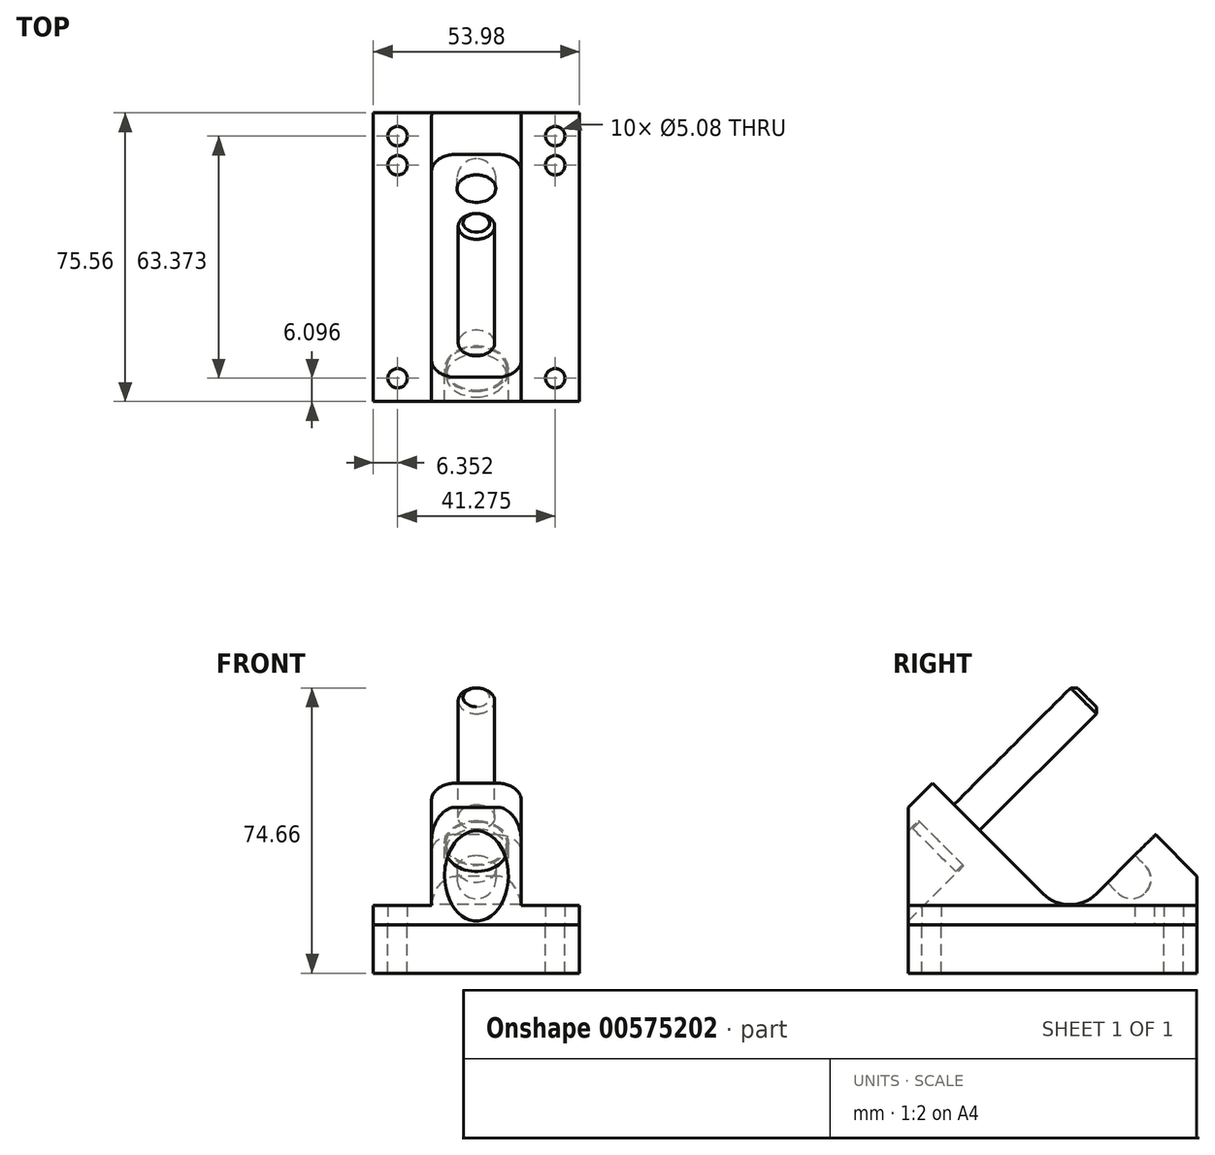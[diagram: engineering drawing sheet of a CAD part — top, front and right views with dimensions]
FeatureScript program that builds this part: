
annotation { "Feature Type Name" : "Feature", "Feature Type Description" : "" }
export const myFeature = defineFeature(function(context is Context, id is Id, definition is map)
    precondition{}
    {
        {
            var Q0;
            Q0=qCreatedBy(makeId("Right.planeOp"),FACE);
            var sketch = newSketch(context, id + "F0", { "sketchPlane" : qUnion([Q0])});
            skLineSegment(sketch, "E0", {"start": v(0, 0) * mm, "end": v(75.57, 0) * mm});
            skLineSegment(sketch, "E1", {"start": v(75.57, 0) * mm, "end": v(75.57, 12.7) * mm});
            skLineSegment(sketch, "E2", {"start": v(75.57, 12.7) * mm, "end": v(64.7, 23.57) * mm});
            skLineSegment(sketch, "E3", {"start": v(64.7, 23.57) * mm, "end": v(42.25, 1.12) * mm});
            skLineSegment(sketch, "E4", {"start": v(0, -14.12) * mm, "end": v(0, 0) * mm, "construction": true});
            skLineSegment(sketch, "E5", {"start": v(0, 0) * mm, "end": v(0, 30.72) * mm});
            skLineSegment(sketch, "E6", {"start": v(0, 30.72) * mm, "end": v(6.32, 37.04) * mm});
            skLineSegment(sketch, "E7", {"start": v(6.32, 37.04) * mm, "end": v(42.25, 1.12) * mm});
            skLineSegment(sketch, "E8", {"start": v(61.1, 19.98) * mm, "end": v(70.08, 11) * mm, "construction": true});
            skLineSegment(sketch, "E9", {"start": v(70.08, 11) * mm, "end": v(59.3, 0.22) * mm, "construction": true});
            skLineSegment(sketch, "E10", {"start": v(59.3, 0.22) * mm, "end": v(50.33, 9.2) * mm, "construction": true});
            skLineSegment(sketch, "E11", {"start": v(64.7, 5.6) * mm, "end": v(15.3, 55) * mm, "construction": true});
            skCircle(sketch, "E12", {"center": v(15.3, 55) * mm, "radius": 4 * mm, "construction": true});
            skLineSegment(sketch, "E13", {"start": v(15.3, 28.06) * mm, "end": v(28.77, 41.53) * mm, "construction": true});
            skCircle(sketch, "E14", {"center": v(58.4, 11.9) * mm, "radius": 5.08 * mm, "construction": true});
            skSolve(sketch);
        }
        {
            var Q0;
            Q0=qSketchRegion(id+"F0",true);
            extrude(context, id + "F1", {"entities" : qUnion([Q0]), "depth" : 26.99 * mm});
        }
        {
            var Q0;
            Q0=makeQuery(id+"F1.opExtrude","SWEPT_EDGE",EDGE,{"disambiguationData":[OSD([sQuery(id+"F0.wireOp",EDGE,"E3"),sQuery(id+"F0.wireOp",EDGE,"E7")])]});
            fillet(context, id + "F2", {"entities" : qUnion([Q0]), "radius" : 9.9 * mm, "tangentPropagation" : true, "allowEdgeOverflow" : false});
        }
        {
            var Q0;
            Q0=makeQuery(id+"F1.opExtrude","CAP_FACE",FACE,{"disambiguationData":[OSD([sQuery(id+"F0.wireOp",EDGE,"E0"),sQuery(id+"F0.wireOp",EDGE,"E1"),sQuery(id+"F0.wireOp",EDGE,"E2"),sQuery(id+"F0.wireOp",EDGE,"E3"),sQuery(id+"F0.wireOp",EDGE,"O8t1L6aE-7V4B-qQYz-aJHa-yxt4Uf4GNHZm"),sQuery(id+"F0.wireOp",EDGE,"dINw5n4X-CGaa-rPGi-QK1T-MrZfrRMsY7ox"),sQuery(id+"F0.wireOp",EDGE,"k2Hi1M4v-dZXO-cidX-ee3S-7WINr6mVTnzP")])],"isStart":false});
            var sketch = newSketch(context, id + "F3", { "sketchPlane" : qUnion([Q0])});
            skLineSegment(sketch, "E15.bottom", {"start": v(75.57, 5.08) * mm, "end": v(0, 5.08) * mm});
            skLineSegment(sketch, "E15.top", {"start": v(75.57, 37.04) * mm, "end": v(0, 37.04) * mm});
            skLineSegment(sketch, "E15.left", {"start": v(75.57, 5.08) * mm, "end": v(75.57, 37.04) * mm});
            skLineSegment(sketch, "E15.right", {"start": v(0, 5.08) * mm, "end": v(0, 37.04) * mm});
            skSolve(sketch);
        }
        {
            var Q0;
            Q0=qSketchRegion(id+"F3",true);
            extrude(context, id + "F4", {"entities" : qUnion([Q0]), "operationType" : NewBodyOperationType.REMOVE, "oppositeDirection" : true, "depth" : 15.24 * mm});
        }
        {
            var Q0;
            Q0=makeQuery(id+"F1.opExtrude","SWEPT_FACE",FACE,{"disambiguationData":[OSD([sQuery(id+"F0.wireOp",EDGE,"E0")])]});
            var sketch = newSketch(context, id + "F5", { "sketchPlane" : qUnion([Q0])});
            skLineSegment(sketch, "E16", {"start": v(20.64, -6.1) * mm, "end": v(20.64, -61.85) * mm, "construction": true});
            skLineSegment(sketch, "E17", {"start": v(20.64, -61.85) * mm, "end": v(20.64, -69.47) * mm, "construction": true});
            skCircle(sketch, "E18", {"center": v(20.64, -6.1) * mm, "radius": 2.54 * mm});
            skCircle(sketch, "E19", {"center": v(20.64, -61.85) * mm, "radius": 2.54 * mm});
            skCircle(sketch, "E20", {"center": v(20.64, -69.47) * mm, "radius": 2.54 * mm});
            skSolve(sketch);
        }
        {
            var Q0;
            Q0=qSketchRegion(id+"F5",true);
            extrude(context, id + "F6", {"entities" : qUnion([Q0]), "operationType" : NewBodyOperationType.REMOVE, "endBound" : BoundingType.UP_TO_NEXT, "oppositeDirection" : true, "depth" : 25.4 * mm});
        }
        {
            var Q0;
            Q0=makeQuery(id+"F1.opExtrude","CAP_FACE",FACE,{"disambiguationData":[OSD([sQuery(id+"F0.wireOp",EDGE,"E0"),sQuery(id+"F0.wireOp",EDGE,"E1"),sQuery(id+"F0.wireOp",EDGE,"E2"),sQuery(id+"F0.wireOp",EDGE,"E3"),sQuery(id+"F0.wireOp",EDGE,"O8t1L6aE-7V4B-qQYz-aJHa-yxt4Uf4GNHZm"),sQuery(id+"F0.wireOp",EDGE,"dINw5n4X-CGaa-rPGi-QK1T-MrZfrRMsY7ox"),sQuery(id+"F0.wireOp",EDGE,"k2Hi1M4v-dZXO-cidX-ee3S-7WINr6mVTnzP")])],"isStart":true});
            var sketch = newSketch(context, id + "F7", { "sketchPlane" : qUnion([Q0])});
            skLineSegment(sketch, "E21", {"start": v(-11.94, 31.43) * mm, "end": v(-5.2, 24.7) * mm});
            skLineSegment(sketch, "E22", {"start": v(-5.2, 24.7) * mm, "end": v(-2.67, 27.22) * mm});
            skLineSegment(sketch, "E23", {"start": v(-2.67, 27.22) * mm, "end": v(12.28, 12.28) * mm});
            skLineSegment(sketch, "E24", {"start": v(12.28, 12.28) * mm, "end": v(6.38, 6.38) * mm});
            skLineSegment(sketch, "E25", {"start": v(6.38, 6.38) * mm, "end": v(-15.3, 28.06) * mm});
            skLineSegment(sketch, "E26", {"start": v(-15.3, 28.06) * mm, "end": v(-16.61, 29.37) * mm, "construction": true});
            skLineSegment(sketch, "E27", {"start": v(-15.3, 28.06) * mm, "end": v(-11.94, 31.43) * mm});
            skLineSegment(sketch, "E28", {"start": v(0, 0) * mm, "end": v(6.38, 6.38) * mm});
            skSolve(sketch);
        }
        {
            var Q0;
            Q0=qSketchRegion(id+"F7",true);
            var Q1;
            Q1=sQuery(id+"F7.wireOp",EDGE,"E25");
            revolve(context, id + "F8", {"operationType" : NewBodyOperationType.REMOVE, "entities" : qUnion([Q0]), "axis" : qUnion([Q1]), "revolveType" : RevolveType.FULL, "oppositeDirection" : true});
        }
        {
            var Q0;
            Q0=qCreatedBy(makeId("Right.planeOp"),FACE);
            var sketch = newSketch(context, id + "F9", { "sketchPlane" : qUnion([Q0])});
            skLineSegment(sketch, "E29", {"start": v(2.96, 26.94) * mm, "end": v(5.2, 24.7) * mm});
            skLineSegment(sketch, "E30", {"start": v(5.2, 24.7) * mm, "end": v(43.37, 62.86) * mm});
            skLineSegment(sketch, "E31", {"start": v(43.37, 62.86) * mm, "end": v(46.74, 59.5) * mm});
            skLineSegment(sketch, "E32", {"start": v(46.74, 59.5) * mm, "end": v(6.77, 19.53) * mm});
            skLineSegment(sketch, "E33", {"start": v(6.77, 19.53) * mm, "end": v(1.16, 25.14) * mm});
            skLineSegment(sketch, "E34", {"start": v(1.16, 25.14) * mm, "end": v(2.96, 26.94) * mm});
            skLineSegment(sketch, "E35", {"start": v(6.77, 19.53) * mm, "end": v(2.3, 15.06) * mm, "construction": true});
            skPoint(sketch, "E36", {"position": v(8.78, 21.53) * mm});
            skSolve(sketch);
        }
        {
            var Q0;
            Q0=qSketchRegion(id+"F9",true);
            var Q1;
            Q1=sQuery(id+"F9.wireOp",EDGE,"E32");
            revolve(context, id + "F10", {"entities" : qUnion([Q0]), "axis" : qUnion([Q1]), "revolveType" : RevolveType.FULL});
        }
        {
            var Q0;
            Q0=makeQuery(id+"F4.boolean.opBoolean","INTERSECT",EDGE,{"derivedFrom":[makeQuery(id+"F1.opExtrude","SWEPT_FACE",FACE,{"disambiguationData":[OSD([sQuery(id+"F0.wireOp",EDGE,"E2")])]}),makeQuery(id+"F4.opExtrude","CAP_FACE",FACE,{"disambiguationData":[OSD([sQuery(id+"F3.wireOp",EDGE,"E15.bottom"),sQuery(id+"F3.wireOp",EDGE,"E15.top"),sQuery(id+"F3.wireOp",EDGE,"E15.left"),sQuery(id+"F3.wireOp",EDGE,"E15.right")])],"isStart":false})]});
            var Q1;
            Q1=makeQuery(id+"FPWNDdPn0RB2iZ7_1.opPattern","COPY",EDGE,{"derivedFrom":makeQuery(id+"F4.boolean.opBoolean","INTERSECT",EDGE,{"derivedFrom":[makeQuery(id+"F1.opExtrude","SWEPT_FACE",FACE,{"disambiguationData":[OSD([sQuery(id+"F0.wireOp",EDGE,"E2")])]}),makeQuery(id+"F4.opExtrude","CAP_FACE",FACE,{"disambiguationData":[OSD([sQuery(id+"F3.wireOp",EDGE,"E15.bottom"),sQuery(id+"F3.wireOp",EDGE,"E15.top"),sQuery(id+"F3.wireOp",EDGE,"E15.left"),sQuery(id+"F3.wireOp",EDGE,"E15.right")])],"isStart":false})]}),"instanceName":"1"});
            var Q2;
            Q2=makeQuery(id+"F4.boolean.opBoolean","INTERSECT",EDGE,{"derivedFrom":[makeQuery(id+"F1.opExtrude","SWEPT_FACE",FACE,{"disambiguationData":[OSD([sQuery(id+"F0.wireOp",EDGE,"E6")])]}),makeQuery(id+"F4.opExtrude","CAP_FACE",FACE,{"disambiguationData":[OSD([sQuery(id+"F3.wireOp",EDGE,"E15.bottom"),sQuery(id+"F3.wireOp",EDGE,"E15.top"),sQuery(id+"F3.wireOp",EDGE,"E15.left"),sQuery(id+"F3.wireOp",EDGE,"E15.right")])],"isStart":false})]});
            var Q3;
            Q3=makeQuery(id+"FPWNDdPn0RB2iZ7_1.opPattern","COPY",EDGE,{"derivedFrom":makeQuery(id+"F4.boolean.opBoolean","INTERSECT",EDGE,{"derivedFrom":[makeQuery(id+"F1.opExtrude","SWEPT_FACE",FACE,{"disambiguationData":[OSD([sQuery(id+"F0.wireOp",EDGE,"E6")])]}),makeQuery(id+"F4.opExtrude","CAP_FACE",FACE,{"disambiguationData":[OSD([sQuery(id+"F3.wireOp",EDGE,"E15.bottom"),sQuery(id+"F3.wireOp",EDGE,"E15.top"),sQuery(id+"F3.wireOp",EDGE,"E15.left"),sQuery(id+"F3.wireOp",EDGE,"E15.right")])],"isStart":false})]}),"instanceName":"1"});
            fillet(context, id + "F11", {"entities" : qUnion([Q0, Q1, Q2, Q3]), "radius" : 6.35 * mm, "tangentPropagation" : true, "allowEdgeOverflow" : false});
        }
        {
            var Q0;
            Q0=qCreatedBy(makeId("Right.planeOp"),FACE);
            var sketch = newSketch(context, id + "F12", { "sketchPlane" : qUnion([Q0])});
            skLineSegment(sketch, "E37.0", {"start": v(61.1, 19.98) * mm, "end": v(70.08, 11) * mm});
            skLineSegment(sketch, "E37.1", {"start": v(70.08, 11) * mm, "end": v(64.7, 5.6) * mm});
            skLineSegment(sketch, "E37.2", {"start": v(64.7, 5.6) * mm, "end": v(55.72, 14.59) * mm});
            skLineSegment(sketch, "E38", {"start": v(61.1, 19.98) * mm, "end": v(55.72, 14.59) * mm});
            skPoint(sketch, "E39.orphan", {"position": v(15.3, 55) * mm});
            skPoint(sketch, "E40.orphan", {"position": v(59.3, 0.22) * mm});
            skSolve(sketch);
        }
        {
            var Q0;
            Q0=qSketchRegion(id+"F12",true);
            var Q1;
            Q1=sQuery(id+"F12.wireOp",EDGE,"E37.2");
            revolve(context, id + "F13", {"operationType" : NewBodyOperationType.REMOVE, "entities" : qUnion([Q0]), "axis" : qUnion([Q1]), "revolveType" : RevolveType.FULL, "oppositeDirection" : true});
        }
        {
            var Q0;
            Q0=qCreatedBy(makeId("Right.planeOp"),FACE);
            var sketch = newSketch(context, id + "F14", { "sketchPlane" : qUnion([Q0])});
            skLineSegment(sketch, "E41.0", {"start": v(61.1, 19.98) * mm, "end": v(70.08, 11) * mm});
            skLineSegment(sketch, "E41.1", {"start": v(70.08, 11) * mm, "end": v(64.7, 5.6) * mm});
            skLineSegment(sketch, "E41.2", {"start": v(64.7, 5.6) * mm, "end": v(62, 8.3) * mm});
            skArc(sketch, "E41.3", {"start": v(62, 8.3) * mm, "mid": v(63.49, 11.9) * mm, "end": v(62, 15.49) * mm});
            skLineSegment(sketch, "E42", {"start": v(62, 15.49) * mm, "end": v(59.3, 18.18) * mm});
            skLineSegment(sketch, "E43", {"start": v(59.3, 18.18) * mm, "end": v(61.1, 19.98) * mm});
            skPoint(sketch, "E44.orphan", {"position": v(15.3, 55) * mm});
            skPoint(sketch, "E45.orphan", {"position": v(59.3, 0.22) * mm});
            skSolve(sketch);
        }
        {
            var Q0;
            Q0=qSketchRegion(id+"F14",true);
            var Q1;
            Q1=sQuery(id+"F0.wireOp",EDGE,"E11");
            revolve(context, id + "F15", {"entities" : qUnion([Q0]), "axis" : qUnion([Q1]), "revolveType" : RevolveType.FULL});
        }
        {
            var Q0;
            Q0=makeQuery(id+"F1.opExtrude","SWEPT_BODY",BODY,{"disambiguationData":[OSD([sQuery(id+"F0.wireOp",EDGE,"E0"),sQuery(id+"F0.wireOp",EDGE,"E1"),sQuery(id+"F0.wireOp",EDGE,"E2"),sQuery(id+"F0.wireOp",EDGE,"E3"),sQuery(id+"F0.wireOp",EDGE,"E5"),sQuery(id+"F0.wireOp",EDGE,"E6"),sQuery(id+"F0.wireOp",EDGE,"E7")])]});
            var Q1;
            Q1=qCreatedBy(makeId("Right.planeOp"),FACE);
            mirror(context, id + "F16", {"operationType" : NewBodyOperationType.ADD, "entities" : qUnion([Q0]), "mirrorPlane" : qUnion([Q1])});
        }
        {
            var Q0;
            Q0=makeQuery(id+"F10.opRevolve","SWEPT_EDGE",EDGE,{"disambiguationData":[OSD([sQuery(id+"F9.wireOp",EDGE,"E30"),sQuery(id+"F9.wireOp",EDGE,"E31")])]});
            chamfer(context, id + "F17", {"entities" : qUnion([Q0]), "width" : 1.27 * mm, "tangentPropagation" : true});
        }
        {
            var Q0;
            {var subQ0=makeQuery(id+"F1.opExtrude","SWEPT_FACE",FACE,{"disambiguationData":[OSD([sQuery(id+"F0.wireOp",EDGE,"E0")])]});Q0=makeQuery(id+"F16.boolean.opBoolean","MERGE",FACE,{"derivedFrom":[subQ0,makeQuery(id+"F16.opPattern","COPY",FACE,{"derivedFrom":subQ0,"instanceName":"1"})]});}
            var sketch = newSketch(context, id + "F18", { "sketchPlane" : qUnion([Q0])});
            skLineSegment(sketch, "E46.0", {"start": v(26.99, 0) * mm, "end": v(-26.99, 0) * mm});
            skLineSegment(sketch, "E46.1", {"start": v(26.99, 0) * mm, "end": v(26.99, -75.57) * mm});
            skLineSegment(sketch, "E46.2", {"start": v(26.99, -75.57) * mm, "end": v(-26.99, -75.57) * mm});
            skLineSegment(sketch, "E46.3", {"start": v(-26.99, 0) * mm, "end": v(-26.99, -75.57) * mm});
            skCircle(sketch, "E46.4", {"center": v(-20.64, -69.47) * mm, "radius": 2.54 * mm});
            skCircle(sketch, "E46.5", {"center": v(20.64, -69.47) * mm, "radius": 2.54 * mm});
            skCircle(sketch, "E46.6", {"center": v(20.64, -6.1) * mm, "radius": 2.54 * mm});
            skCircle(sketch, "E46.7", {"center": v(-20.64, -6.1) * mm, "radius": 2.54 * mm});
            skSolve(sketch);
        }
        {
            var Q0;
            Q0=qSketchRegion(id+"F18",true);
            extrude(context, id + "F19", {"entities" : qUnion([Q0]), "depth" : 12.7 * mm, "offsetDistance" : 25.4 * mm});
        }
    });
